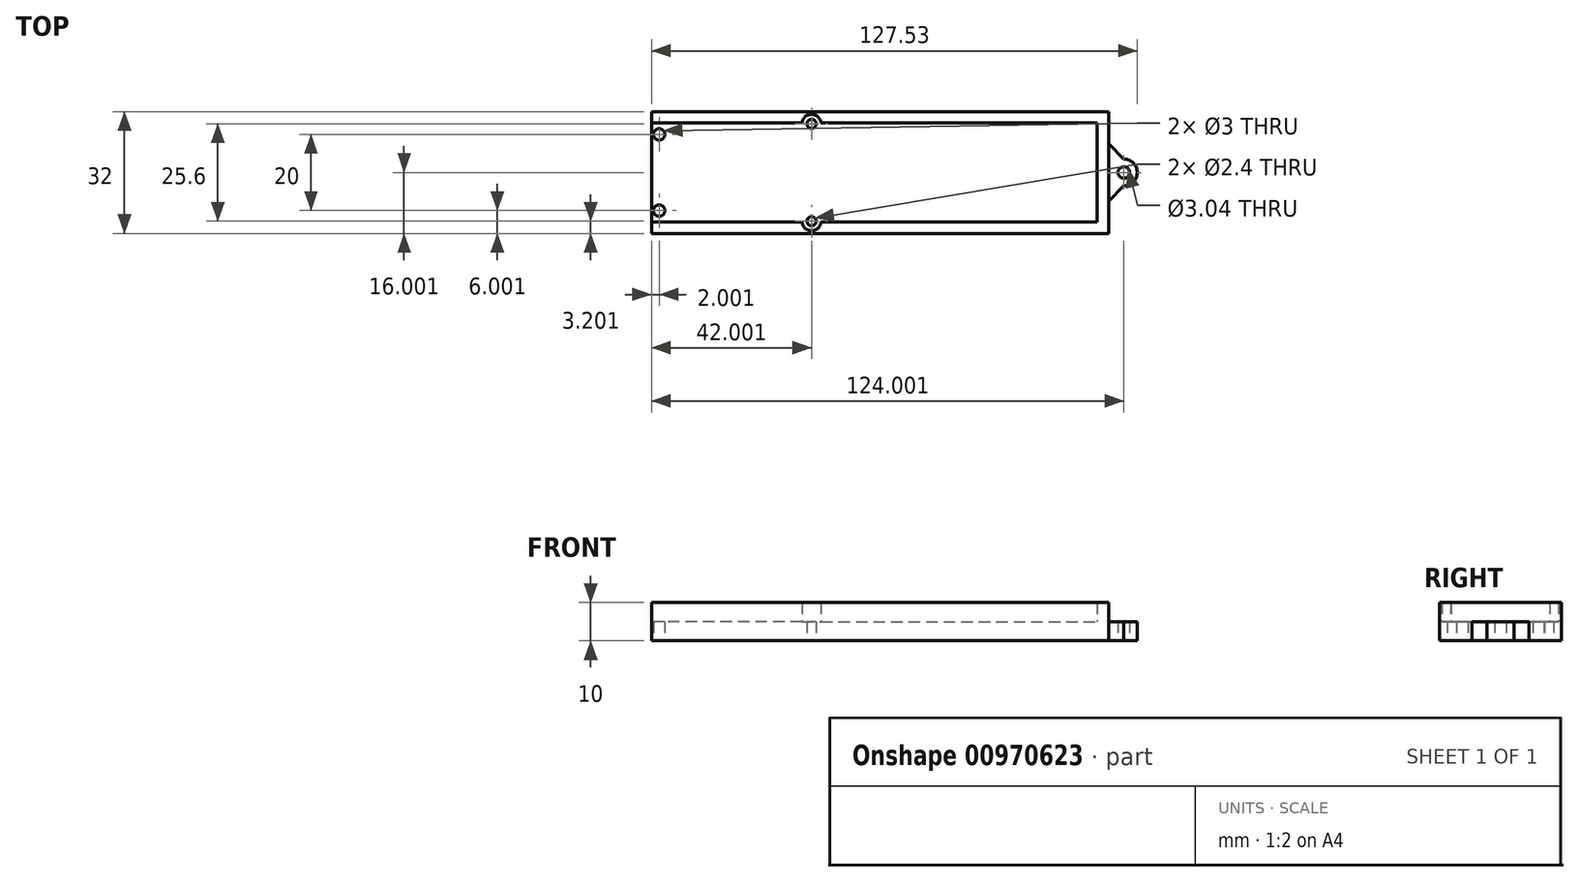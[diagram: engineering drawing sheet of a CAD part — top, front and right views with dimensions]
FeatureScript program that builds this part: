
annotation { "Feature Type Name" : "Feature", "Feature Type Description" : "" }
export const myFeature = defineFeature(function(context is Context, id is Id, definition is map)
    precondition{}
    {
        {
            var Q0;
            Q0=qCreatedBy(makeId("Top.planeOp"),FACE);
            var sketch = newSketch(context, id + "F0", { "sketchPlane" : qUnion([Q0])});
            skLineSegment(sketch, "E0.left", {"start": v(-44.95, 2.45) * mm, "end": v(-44.95, -29.55) * mm});
            skLineSegment(sketch, "E1", {"start": v(-44.95, -13.55) * mm, "end": v(75.05, -13.55) * mm, "construction": true});
            skCircle(sketch, "E2", {"center": v(-2.95, -0.75) * mm, "radius": 1.2 * mm});
            skCircle(sketch, "E3.MirrorC", {"center": v(-2.95, -26.35) * mm, "radius": 1.2 * mm});
            skLineSegment(sketch, "E4", {"start": v(-44.95, 2.45) * mm, "end": v(75.05, 2.45) * mm});
            skLineSegment(sketch, "E5", {"start": v(75.05, 2.45) * mm, "end": v(75.05, -29.55) * mm});
            skLineSegment(sketch, "E6", {"start": v(75.05, -29.55) * mm, "end": v(-44.95, -29.55) * mm});
            skArc(sketch, "E7", {"start": v(-0.46, -0.55) * mm, "mid": v(-2.96, 1.75) * mm, "end": v(-5.44, -0.57) * mm});
            skLineSegment(sketch, "E8", {"start": v(-5.44, -0.57) * mm, "end": v(-44.95, -0.57) * mm});
            skLineSegment(sketch, "E9", {"start": v(-0.46, -0.55) * mm, "end": v(72.05, -0.55) * mm});
            skLineSegment(sketch, "E10", {"start": v(72.05, -0.55) * mm, "end": v(72.05, -13.55) * mm});
            skLineSegment(sketch, "E11.MirrorCS", {"start": v(-0.46, -26.55) * mm, "end": v(72.05, -26.55) * mm});
            skArc(sketch, "E12.MirrorCS", {"start": v(-0.46, -26.55) * mm, "mid": v(-2.96, -28.85) * mm, "end": v(-5.44, -26.53) * mm});
            skLineSegment(sketch, "E13.MirrorCS", {"start": v(-5.44, -26.53) * mm, "end": v(-44.95, -26.53) * mm});
            skLineSegment(sketch, "E14.MirrorCS", {"start": v(72.05, -26.55) * mm, "end": v(72.05, -13.55) * mm});
            skCircle(sketch, "E15", {"center": v(-42.95, -3.55) * mm, "radius": 1.5 * mm});
            skCircle(sketch, "E16.MirrorC", {"center": v(-42.95, -23.55) * mm, "radius": 1.5 * mm});
            skLineSegment(sketch, "E17", {"start": v(75.05, -13.55) * mm, "end": v(87.24, -13.55) * mm, "construction": true});
            skCircle(sketch, "E18", {"center": v(79.05, -13.55) * mm, "radius": 1.52 * mm});
            skArc(sketch, "E19", {"start": v(79.05, -17.08) * mm, "mid": v(82.58, -13.55) * mm, "end": v(79.05, -10.02) * mm});
            skLineSegment(sketch, "E20", {"start": v(79.05, -10.02) * mm, "end": v(75.05, -6.02) * mm});
            skLineSegment(sketch, "E21.MirrorCS", {"start": v(79.05, -17.08) * mm, "end": v(75.05, -21.08) * mm});
            skSolve(sketch);
        }
        {
            var Q0;
            {var subQ2=sQuery(id+"F0.wireOp",EDGE,"E4");Q0=makeQuery(id+"F0.imprint","IMPRINT",FACE,{"disambiguationData":[TD([[makeQuery(id+"F0.imprint","IMPRINT",EDGE,{"derivedFrom":subQ2}),-1.0]])]});}
            extrude(context, id + "F1", {"entities" : qUnion([Q0]), "depth" : 10 * mm, "offsetDistance" : 25 * mm});
        }
        {
            var Q0;
            Q0=makeQuery(id+"F0.imprint","IMPRINT",FACE,{"disambiguationData":[TD([[makeQuery(id+"F0.imprint","IMPRINT",EDGE,{"derivedFrom":sQuery(id+"F0.wireOp",EDGE,"E2")}),-1.0]])]});
            var Q1;
            Q1=makeQuery(id+"F0.imprint","IMPRINT",FACE,{"disambiguationData":[TD([[makeQuery(id+"F0.imprint","IMPRINT",EDGE,{"derivedFrom":sQuery(id+"F0.wireOp",EDGE,"E18")}),-1.0]])]});
            extrude(context, id + "F2", {"entities" : qUnion([Q0, Q1]), "operationType" : NewBodyOperationType.ADD, "depth" : 5 * mm, "offsetDistance" : 25 * mm});
        }
    });
